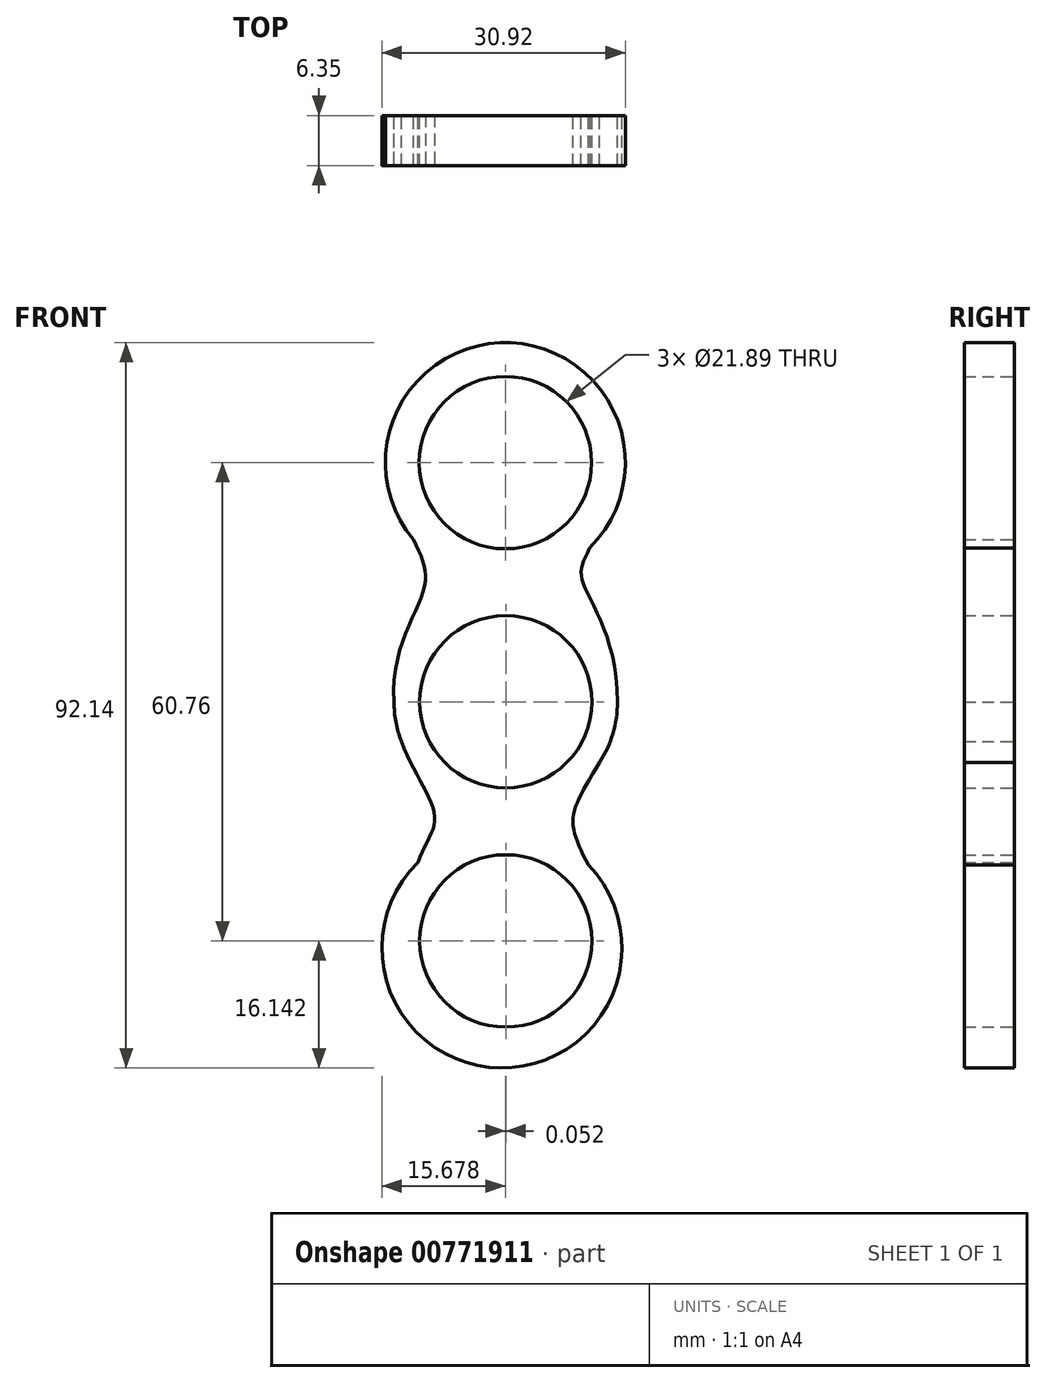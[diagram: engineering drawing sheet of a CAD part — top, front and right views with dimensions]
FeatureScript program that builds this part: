
annotation { "Feature Type Name" : "Feature", "Feature Type Description" : "" }
export const myFeature = defineFeature(function(context is Context, id is Id, definition is map)
    precondition{}
    {
        {
            var Q0;
            Q0=qCreatedBy(makeId("Front.planeOp"),FACE);
            var sketch = newSketch(context, id + "F0", { "sketchPlane" : qUnion([Q0])});
            skCircle(sketch, "E0", {"center": v(0, 0) * mm, "radius": 10.95 * mm});
            skArc(sketch, "E1", {"start": v(10.64, 19.52) * mm, "mid": v(0.68, 45.6) * mm, "end": v(-11.74, 20.6) * mm});
            skCircle(sketch, "E2", {"center": v(-0.05, 30.38) * mm, "radius": 10.95 * mm});
            skCircle(sketch, "E3", {"center": v(0, 0) * mm, "radius": 14.2 * mm});
            skFitSpline(sketch, "E4", {"points": [v(-14.2, 0) * mm, v(-10.3, 14.81) * mm, v(-11.74, 20.6) * mm], "startDerivative": vector(-2.6, 33.68) * mm, "endDerivative": vector(-8.14, 16.97) * mm});
            skFitSpline(sketch, "E5", {"points": [v(14.2, 0) * mm, v(9.64, 15.76) * mm, v(10.64, 19.52) * mm], "startDerivative": vector(0, 38.16) * mm, "endDerivative": vector(6.72, 15) * mm});
            skLineSegment(sketch, "E6", {"start": v(14.2, 0) * mm, "end": v(25.8, 0) * mm, "construction": true});
            skLineSegment(sketch, "E7", {"start": v(0, 0) * mm, "end": v(0, -30.38) * mm});
            skCircle(sketch, "E8", {"center": v(0, -30.38) * mm, "radius": 10.95 * mm});
            skArc(sketch, "E9", {"start": v(-11.17, -20.42) * mm, "mid": v(-0.7, -46.52) * mm, "end": v(10.5, -20.71) * mm});
            skFitSpline(sketch, "E10", {"points": [v(-11.17, -20.42) * mm, v(-9.04, -14.58) * mm, v(-13.27, -5.04) * mm], "startDerivative": vector(6.18, 17.07) * mm, "endDerivative": vector(-7.46, 20.5) * mm});
            skFitSpline(sketch, "E11", {"points": [v(10.5, -20.71) * mm, v(8.56, -14.82) * mm, v(12.37, -6.96) * mm], "startDerivative": vector(-8.53, 16.25) * mm, "endDerivative": vector(11.81, 19.6) * mm});
            skSolve(sketch);
        }
        {
            var Q0;
            Q0 = qSketchRegion(id + "F0", true);
            extrude(context, id + "F1", {"entities" : qUnion([Q0]), "depth" : 6.35 * mm, "offsetDistance" : 25.4 * mm});
        }
    });
